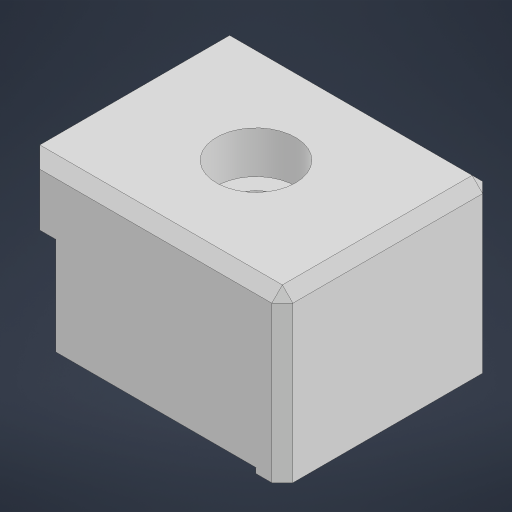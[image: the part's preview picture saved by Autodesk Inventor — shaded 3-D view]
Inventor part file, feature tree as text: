
AUTODESK INVENTOR PART (.ipt)
format: ipt  version: 2024.1 (Build 281209000, 209)  size: 181,760 bytes
history: native  units: mm
features: chamfer x2, sketch x2, extrude x1, hole x1, projected_geometry x1
ambient origin geometry x8: Origin, YZ Plane, XZ Plane, XY Plane, X Axis, Y Axis, Z Axis, Center Point
bodies: Solid1 (feature_tree)
feature tree (7):
  extrude  "Extrusion1"  Depth=31.5mm
  hole  "Hole1"  [1 undecoded]
  chamfer  "Chamfer1"  Distance=5.0mm
  chamfer  "Chamfer2"  Distance=40.0mm
  sketch  "Sketch1"  dims[d0=50.0mm d1=31.5mm]
  sketch  "Sketch2"  dims[d2=1.0mm d3=7.0mm d5=5.0mm d6=40.0mm d7=0.0mm d8=8.5mm d9=6.0mm d10=15.0mm d11=8.0mm d12=90.0deg d13=8.0mm d14=20.594885mm d15=2.0mm d16=2.0mm d17=45.0deg d18=4.0mm d19=2.0mm d20=45.0deg d23=18.0mm d24=12.0mm d25=19.5mm d26=38.0mm]
  projected_geometry  "Projected Loop1"
note: 1 required parameter value undecoded (feature->parameter linkage not recoverable at this tier; creation-order binding heuristic only, values carry confidence <= 0.55)
